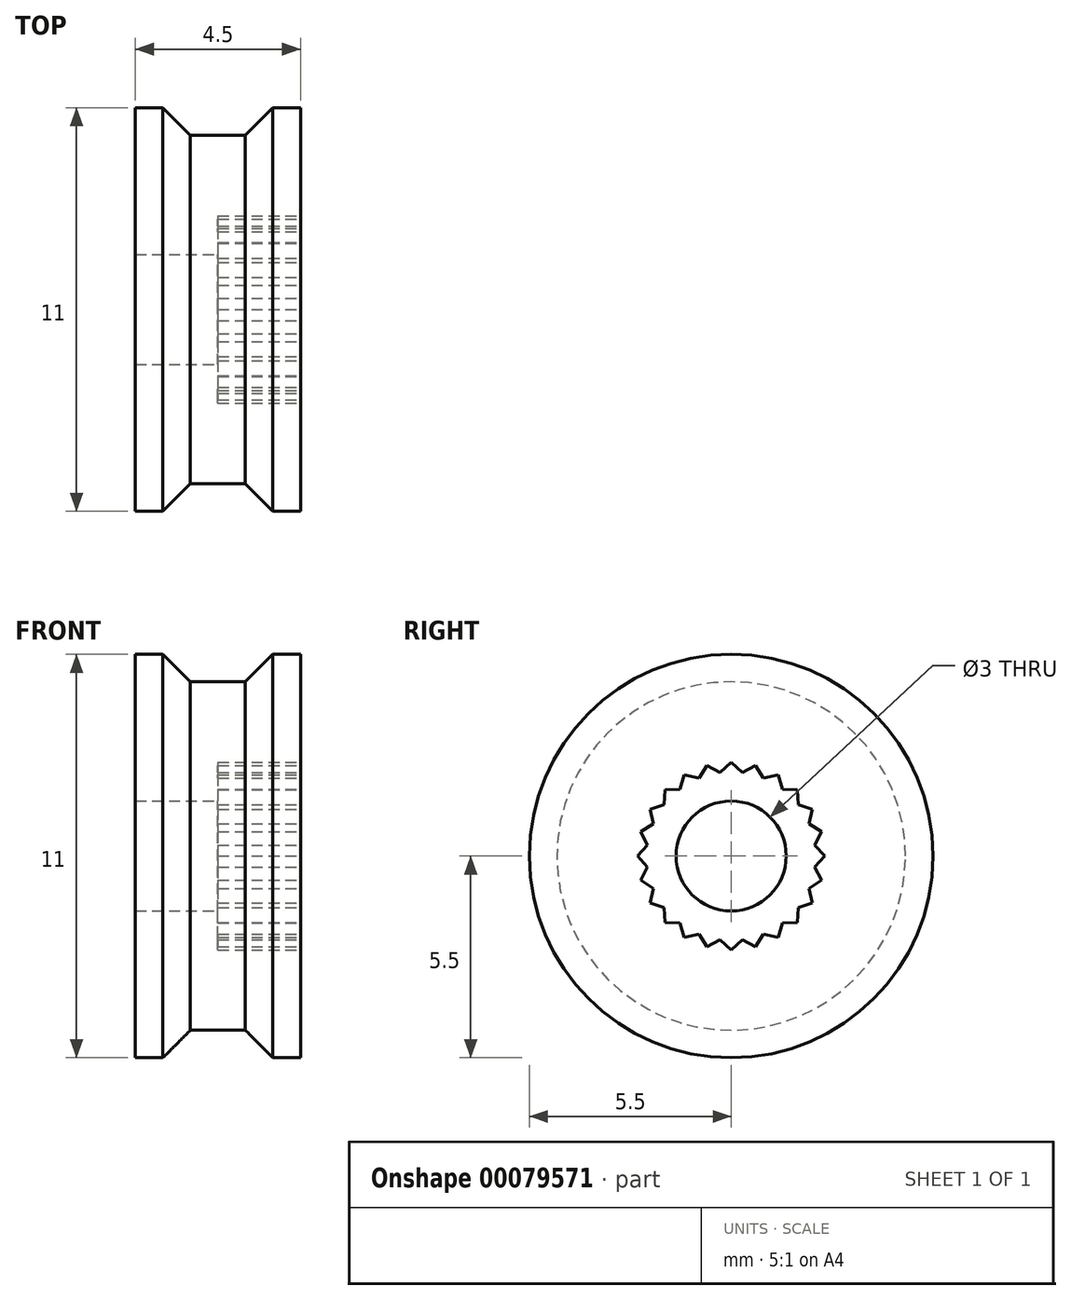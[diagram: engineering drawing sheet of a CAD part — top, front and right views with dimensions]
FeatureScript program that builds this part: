
annotation { "Feature Type Name" : "Feature", "Feature Type Description" : "" }
export const myFeature = defineFeature(function(context is Context, id is Id, definition is map)
    precondition{}
    {
        {
            var Q0;
            Q0=qCreatedBy(makeId("Front.planeOp"),FACE);
            var sketch = newSketch(context, id + "F0", { "sketchPlane" : qUnion([Q0]), "disableImprinting" : false});
            skLineSegment(sketch, "E0", {"start": v(-2.25, 0) * mm, "end": v(-2.25, 6.25) * mm});
            skLineSegment(sketch, "E1", {"start": v(-2.25, 6.25) * mm, "end": v(-0.75, 4.75) * mm});
            skLineSegment(sketch, "E2", {"start": v(-0.75, 4.75) * mm, "end": v(0.75, 4.75) * mm});
            skLineSegment(sketch, "E3", {"start": v(0.75, 4.75) * mm, "end": v(2.25, 6.25) * mm});
            skLineSegment(sketch, "E4", {"start": v(2.25, 6.25) * mm, "end": v(2.25, 0) * mm});
            skLineSegment(sketch, "E5", {"start": v(2.25, 0) * mm, "end": v(-2.25, 0) * mm});
            skPoint(sketch, "E6", {"position": v(0, 0) * mm});
            skLineSegment(sketch, "E7", {"start": v(-2.25, 5.5) * mm, "end": v(2.25, 5.5) * mm});
            skSolve(sketch);
        }
        {
            var Q0;
            {var subQ10=sQuery(id+"F0.wireOp",EDGE,"E2");Q0=makeQuery(id+"F0.imprint","IMPRINT",FACE,{"disambiguationData":[TD([[makeQuery(id+"F0.imprint","IMPRINT",EDGE,{"derivedFrom":subQ10}),-1.0]])]});}
            var Q1;
            Q1=sQuery(id+"F0.wireOp",EDGE,"E5");
            revolve(context, id + "F1", {"entities" : qUnion([Q0]), "axis" : qUnion([Q1]), "revolveType" : RevolveType.FULL});
        }
        {
            var Q0;
            Q0=makeQuery(id+"F1.opRevolve","SWEPT_FACE",FACE,{"disambiguationData":[OSD([sQuery(id+"F0.wireOp",EDGE,"E4")])]});
            var sketch = newSketch(context, id + "F2", { "sketchPlane" : qUnion([Q0])});
            skCircle(sketch, "E8", {"center": v(0, 0) * mm, "radius": 2.3 * mm, "construction": true});
            skFitSpline(sketch, "E9.4", {"points": [v(-0.66, 2.47) * mm, v(-0.54, 2.4) * mm, v(-0.42, 2.34) * mm, v(-0.3, 2.28) * mm]});
            skFitSpline(sketch, "E9.18", {"points": [v(2.28, -0.3) * mm, v(2.34, -0.42) * mm, v(2.4, -0.54) * mm, v(2.47, -0.66) * mm]});
            skFitSpline(sketch, "E9.32", {"points": [v(-0.66, -2.47) * mm, v(-0.73, -2.35) * mm, v(-0.8, -2.24) * mm, v(-0.88, -2.12) * mm]});
            skFitSpline(sketch, "E9.33", {"points": [v(-0.88, -2.12) * mm, v(-1.01, -2.15) * mm, v(-1.15, -2.18) * mm, v(-1.28, -2.21) * mm]});
            skFitSpline(sketch, "E9.7", {"points": [v(0.3, 2.28) * mm, v(0.42, 2.34) * mm, v(0.54, 2.4) * mm, v(0.66, 2.47) * mm]});
            skCircle(sketch, "E10", {"center": v(0, 0) * mm, "radius": 2.56 * mm, "construction": true});
            skFitSpline(sketch, "E9.34", {"points": [v(-1.28, -2.21) * mm, v(-1.32, -2.08) * mm, v(-1.36, -1.95) * mm, v(-1.4, -1.82) * mm]});
            skFitSpline(sketch, "E9.16", {"points": [v(2.47, 0.66) * mm, v(2.4, 0.54) * mm, v(2.34, 0.42) * mm, v(2.28, 0.3) * mm]});
            skFitSpline(sketch, "E9.13", {"points": [v(1.82, 1.4) * mm, v(1.95, 1.36) * mm, v(2.08, 1.32) * mm, v(2.21, 1.28) * mm]});
            skFitSpline(sketch, "E9.25", {"points": [v(1.4, -1.82) * mm, v(1.36, -1.95) * mm, v(1.32, -2.08) * mm, v(1.28, -2.21) * mm]});
            skFitSpline(sketch, "E9.38", {"points": [v(-2.21, -1.28) * mm, v(-2.18, -1.15) * mm, v(-2.15, -1.01) * mm, v(-2.12, -0.88) * mm]});
            skFitSpline(sketch, "E9.14", {"points": [v(2.21, 1.28) * mm, v(2.18, 1.15) * mm, v(2.15, 1.01) * mm, v(2.12, 0.88) * mm]});
            skFitSpline(sketch, "E9.12", {"points": [v(1.8, 1.8) * mm, v(1.81, 1.67) * mm, v(1.82, 1.54) * mm, v(1.82, 1.4) * mm]});
            skFitSpline(sketch, "E9.31", {"points": [v(-0.3, -2.28) * mm, v(-0.42, -2.34) * mm, v(-0.54, -2.4) * mm, v(-0.66, -2.47) * mm]});
            skFitSpline(sketch, "E9.8", {"points": [v(0.66, 2.47) * mm, v(0.73, 2.35) * mm, v(0.8, 2.24) * mm, v(0.88, 2.12) * mm]});
            skFitSpline(sketch, "E9.39", {"points": [v(-2.12, -0.88) * mm, v(-2.24, -0.8) * mm, v(-2.35, -0.73) * mm, v(-2.47, -0.66) * mm]});
            skFitSpline(sketch, "E9.23", {"points": [v(1.82, -1.4) * mm, v(1.82, -1.54) * mm, v(1.81, -1.67) * mm, v(1.8, -1.8) * mm]});
            skFitSpline(sketch, "E9.47", {"points": [v(-2.12, 0.88) * mm, v(-2.15, 1.01) * mm, v(-2.18, 1.15) * mm, v(-2.21, 1.28) * mm]});
            skFitSpline(sketch, "E9.9", {"points": [v(0.88, 2.12) * mm, v(1.01, 2.15) * mm, v(1.15, 2.18) * mm, v(1.28, 2.21) * mm]});
            skFitSpline(sketch, "E9.36", {"points": [v(-1.8, -1.8) * mm, v(-1.81, -1.67) * mm, v(-1.82, -1.54) * mm, v(-1.82, -1.4) * mm]});
            skFitSpline(sketch, "E9.20", {"points": [v(2.47, -0.66) * mm, v(2.35, -0.73) * mm, v(2.24, -0.8) * mm, v(2.12, -0.88) * mm]});
            skFitSpline(sketch, "E9.15", {"points": [v(2.12, 0.88) * mm, v(2.24, 0.8) * mm, v(2.35, 0.73) * mm, v(2.47, 0.66) * mm]});
            skFitSpline(sketch, "E9.2", {"points": [v(-1.28, 2.21) * mm, v(-1.15, 2.18) * mm, v(-1.01, 2.15) * mm, v(-0.88, 2.12) * mm]});
            skFitSpline(sketch, "E9.26", {"points": [v(1.28, -2.21) * mm, v(1.15, -2.18) * mm, v(1.01, -2.15) * mm, v(0.88, -2.12) * mm]});
            skFitSpline(sketch, "E9.30", {"points": [v(0, -2.56) * mm, v(-0.1, -2.46) * mm, v(-0.2, -2.37) * mm, v(-0.3, -2.28) * mm]});
            skFitSpline(sketch, "E9.43", {"points": [v(-2.28, 0.3) * mm, v(-2.34, 0.42) * mm, v(-2.4, 0.54) * mm, v(-2.47, 0.66) * mm]});
            skFitSpline(sketch, "E9.10", {"points": [v(1.28, 2.21) * mm, v(1.32, 2.08) * mm, v(1.36, 1.95) * mm, v(1.4, 1.82) * mm]});
            skFitSpline(sketch, "E9.11", {"points": [v(1.4, 1.82) * mm, v(1.54, 1.82) * mm, v(1.67, 1.81) * mm, v(1.8, 1.8) * mm]});
            skFitSpline(sketch, "E9.35", {"points": [v(-1.4, -1.82) * mm, v(-1.54, -1.82) * mm, v(-1.67, -1.81) * mm, v(-1.8, -1.8) * mm]});
            skFitSpline(sketch, "E9.21", {"points": [v(2.12, -0.88) * mm, v(2.15, -1.01) * mm, v(2.18, -1.15) * mm, v(2.21, -1.28) * mm]});
            skFitSpline(sketch, "E9.37", {"points": [v(-1.82, -1.4) * mm, v(-1.95, -1.36) * mm, v(-2.08, -1.32) * mm, v(-2.21, -1.28) * mm]});
            skFitSpline(sketch, "E9.40", {"points": [v(-2.47, -0.66) * mm, v(-2.4, -0.54) * mm, v(-2.34, -0.42) * mm, v(-2.28, -0.3) * mm]});
            skFitSpline(sketch, "E9.24", {"points": [v(1.8, -1.8) * mm, v(1.67, -1.81) * mm, v(1.54, -1.82) * mm, v(1.4, -1.82) * mm]});
            skFitSpline(sketch, "E9.29", {"points": [v(0.3, -2.28) * mm, v(0.2, -2.37) * mm, v(0.1, -2.46) * mm, v(0, -2.56) * mm]});
            skFitSpline(sketch, "E9.45", {"points": [v(-1.82, 1.4) * mm, v(-1.82, 1.54) * mm, v(-1.81, 1.67) * mm, v(-1.8, 1.8) * mm]});
            skFitSpline(sketch, "E9.41", {"points": [v(-2.28, -0.3) * mm, v(-2.37, -0.2) * mm, v(-2.46, -0.1) * mm, v(-2.56, 0) * mm]});
            skFitSpline(sketch, "E9.44", {"points": [v(-2.47, 0.66) * mm, v(-2.35, 0.73) * mm, v(-2.24, 0.8) * mm, v(-2.12, 0.88) * mm]});
            skFitSpline(sketch, "E9.28", {"points": [v(0.66, -2.47) * mm, v(0.54, -2.4) * mm, v(0.42, -2.34) * mm, v(0.3, -2.28) * mm]});
            skFitSpline(sketch, "E9.0", {"points": [v(-1.8, 1.8) * mm, v(-1.67, 1.81) * mm, v(-1.54, 1.82) * mm, v(-1.4, 1.82) * mm]});
            skFitSpline(sketch, "E9.5", {"points": [v(-0.3, 2.28) * mm, v(-0.2, 2.37) * mm, v(-0.1, 2.46) * mm, v(0, 2.56) * mm]});
            skFitSpline(sketch, "E9.27", {"points": [v(0.88, -2.12) * mm, v(0.8, -2.24) * mm, v(0.73, -2.35) * mm, v(0.66, -2.47) * mm]});
            skFitSpline(sketch, "E9.1", {"points": [v(-1.4, 1.82) * mm, v(-1.36, 1.95) * mm, v(-1.32, 2.08) * mm, v(-1.28, 2.21) * mm]});
            skFitSpline(sketch, "E9.6", {"points": [v(0, 2.56) * mm, v(0.1, 2.46) * mm, v(0.2, 2.37) * mm, v(0.3, 2.28) * mm]});
            skFitSpline(sketch, "E9.22", {"points": [v(2.21, -1.28) * mm, v(2.08, -1.32) * mm, v(1.95, -1.36) * mm, v(1.82, -1.4) * mm]});
            skFitSpline(sketch, "E9.42", {"points": [v(-2.56, 0) * mm, v(-2.46, 0.1) * mm, v(-2.37, 0.2) * mm, v(-2.28, 0.3) * mm]});
            skFitSpline(sketch, "E9.3", {"points": [v(-0.88, 2.12) * mm, v(-0.8, 2.24) * mm, v(-0.73, 2.35) * mm, v(-0.66, 2.47) * mm]});
            skFitSpline(sketch, "E9.17", {"points": [v(2.28, 0.3) * mm, v(2.37, 0.2) * mm, v(2.46, 0.1) * mm, v(2.56, 0) * mm]});
            skFitSpline(sketch, "E9.46", {"points": [v(-2.21, 1.28) * mm, v(-2.08, 1.32) * mm, v(-1.95, 1.36) * mm, v(-1.82, 1.4) * mm]});
            skFitSpline(sketch, "E9.19", {"points": [v(2.56, 0) * mm, v(2.46, -0.1) * mm, v(2.37, -0.2) * mm, v(2.28, -0.3) * mm]});
            skLineSegment(sketch, "E11", {"start": v(-1.82, 1.4) * mm, "end": v(1.82, -1.4) * mm, "construction": true});
            skCircle(sketch, "E12", {"center": v(0, 0) * mm, "radius": 1.5 * mm});
            skSolve(sketch);
        }
        {
            var Q0;
            Q0=makeQuery(id+"F2.imprint","IMPRINT",FACE,{"disambiguationData":[TD([[makeQuery(id+"F2.imprint","IMPRINT",EDGE,{"derivedFrom":sQuery(id+"F2.wireOp",EDGE,"E9.32")}),-1.0]])]});
            var Q1;
            Q1=makeQuery(id+"F2.imprint","IMPRINT",FACE,{"disambiguationData":[TD([[makeQuery(id+"F2.imprint","IMPRINT",EDGE,{"derivedFrom":sQuery(id+"F2.wireOp",EDGE,"E9.4")}),-1.0]])]});
            extrude(context, id + "F3", {"entities" : qUnion([Q0, Q1]), "operationType" : NewBodyOperationType.REMOVE, "oppositeDirection" : true, "depth" : 2.25 * mm});
        }
        {
            var Q0;
            Q0=makeQuery(id+"F2.imprint","IMPRINT",FACE,{"disambiguationData":[TD([[makeQuery(id+"F2.imprint","IMPRINT",EDGE,{"derivedFrom":sQuery(id+"F2.wireOp",EDGE,"E12")}),1.0]])]});
            var Q1;
            Q1=sQuery(id+"F2.wireOp",EDGE,"E12");
            extrude(context, id + "F4", {"entities" : qUnion([Q0]), "operationType" : NewBodyOperationType.REMOVE, "surfaceEntities" : qUnion([Q1]), "endBound" : BoundingType.THROUGH_ALL, "oppositeDirection" : true, "depth" : 25 * mm});
        }
    });
